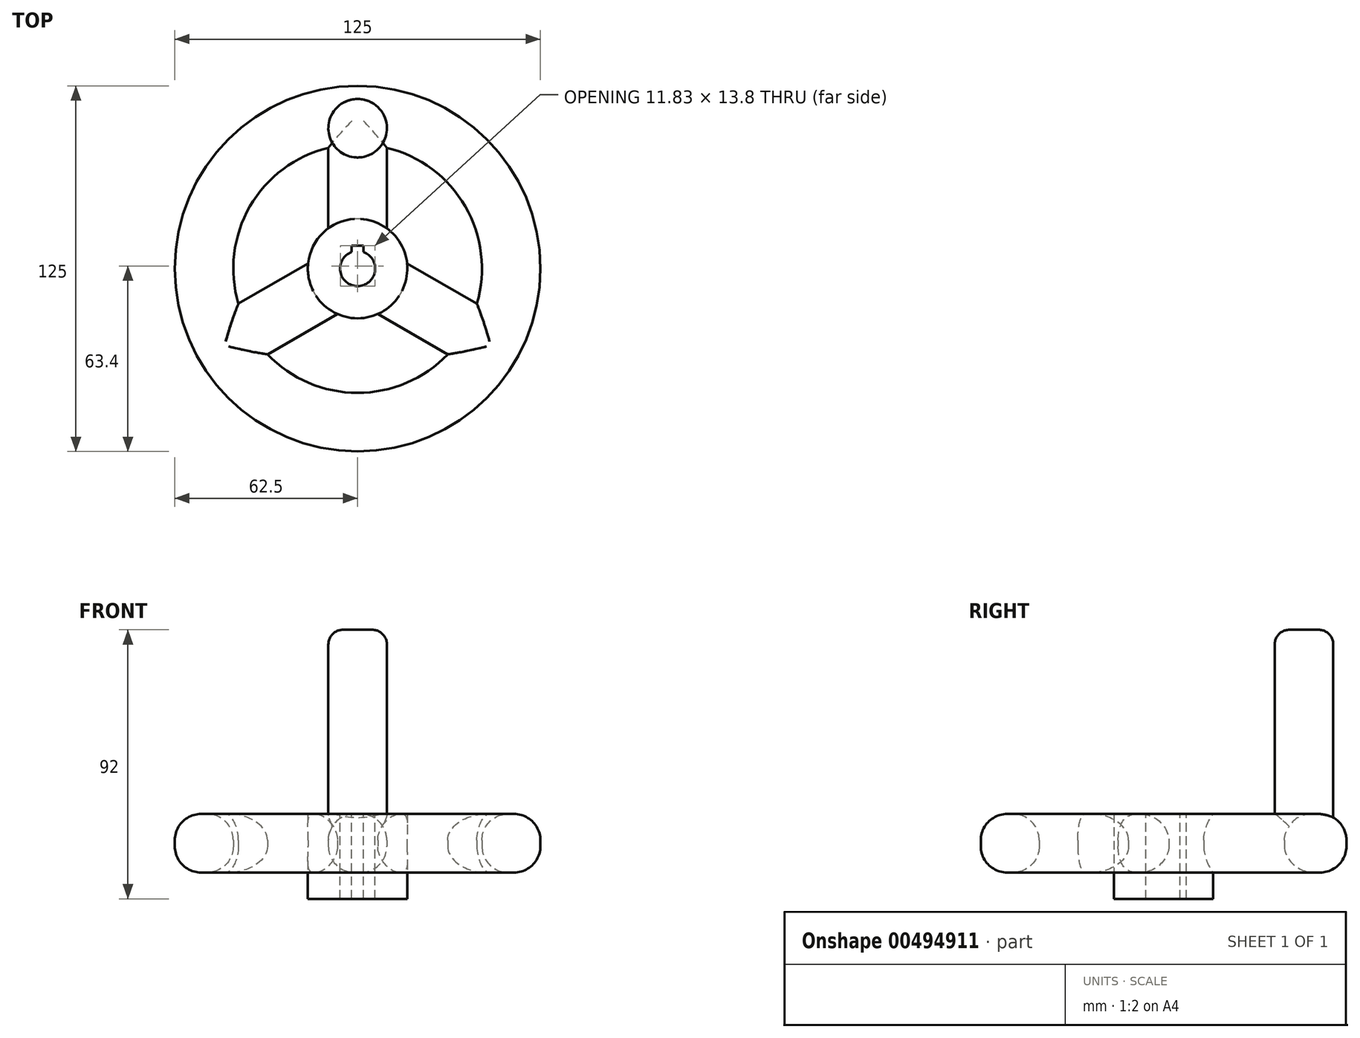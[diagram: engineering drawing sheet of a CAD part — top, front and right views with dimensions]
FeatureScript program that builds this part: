
annotation { "Feature Type Name" : "Feature", "Feature Type Description" : "" }
export const myFeature = defineFeature(function(context is Context, id is Id, definition is map)
    precondition{}
    {
        {
            var Q0;
            Q0=qCreatedBy(makeId("Top.planeOp"),FACE);
            var sketch = newSketch(context, id + "F0", { "sketchPlane" : qUnion([Q0])});
            skArc(sketch, "E0", {"start": v(-6.9, -15.53) * mm, "mid": v(0, -17) * mm, "end": v(6.9, -15.53) * mm});
            skArc(sketch, "E1", {"start": v(-30.77, -29.31) * mm, "mid": v(0, -42.5) * mm, "end": v(30.77, -29.31) * mm});
            skCircle(sketch, "E2", {"center": v(0, 0) * mm, "radius": 62.5 * mm});
            skLineSegment(sketch, "E3", {"start": v(-10, 41.3) * mm, "end": v(-10, 13.75) * mm});
            skLineSegment(sketch, "E4", {"start": v(10, 41.3) * mm, "end": v(10, 13.75) * mm});
            skLineSegment(sketch, "E5", {"start": v(-16.9, 1.79) * mm, "end": v(-40.77, -12) * mm});
            skLineSegment(sketch, "E6", {"start": v(-6.9, -15.53) * mm, "end": v(-30.77, -29.31) * mm});
            skLineSegment(sketch, "E7", {"start": v(6.9, -15.53) * mm, "end": v(30.77, -29.31) * mm});
            skLineSegment(sketch, "E8", {"start": v(16.9, 1.79) * mm, "end": v(40.77, -12) * mm});
            skArc(sketch, "E9.trimOffspring", {"start": v(-10, 13.75) * mm, "mid": v(-14.72, 8.5) * mm, "end": v(-16.9, 1.79) * mm});
            skArc(sketch, "E10.trimOffspring", {"start": v(-10, 41.3) * mm, "mid": v(-36.8, 21.25) * mm, "end": v(-40.77, -12) * mm});
            skArc(sketch, "E11.trimOffspring", {"start": v(40.77, -12) * mm, "mid": v(36.8, 21.25) * mm, "end": v(10, 41.3) * mm});
            skArc(sketch, "E12.trimOffspring", {"start": v(16.9, 1.79) * mm, "mid": v(14.72, 8.5) * mm, "end": v(10, 13.75) * mm});
            skSolve(sketch);
        }
        {
            var Q0;
            Q0=qSketchRegion(id+"F0",true);
            extrude(context, id + "F1", {"entities" : qUnion([Q0]), "depth" : 20 * mm});
        }
        {
            var Q0;
            Q0=makeQuery(id+"F1.opExtrude","CAP_EDGE",EDGE,{"disambiguationData":[OSD([sQuery(id+"F0.wireOp",EDGE,"E5")])],"isStart":false});
            var Q1;
            Q1=makeQuery(id+"F1.opExtrude","CAP_EDGE",EDGE,{"disambiguationData":[OSD([sQuery(id+"F0.wireOp",EDGE,"E8")])],"isStart":false});
            var Q2;
            Q2=makeQuery(id+"F1.opExtrude","CAP_EDGE",EDGE,{"disambiguationData":[OSD([sQuery(id+"F0.wireOp",EDGE,"E7")])],"isStart":false});
            var Q3;
            Q3=makeQuery(id+"F1.opExtrude","CAP_EDGE",EDGE,{"disambiguationData":[OSD([sQuery(id+"F0.wireOp",EDGE,"E6")])],"isStart":false});
            var Q4;
            Q4=makeQuery(id+"F1.opExtrude","CAP_EDGE",EDGE,{"disambiguationData":[OSD([sQuery(id+"F0.wireOp",EDGE,"E1")])],"isStart":false});
            var Q5;
            Q5=makeQuery(id+"F1.opExtrude","CAP_EDGE",EDGE,{"disambiguationData":[OSD([sQuery(id+"F0.wireOp",EDGE,"E5")])],"isStart":true});
            var Q6;
            Q6=makeQuery(id+"F1.opExtrude","CAP_EDGE",EDGE,{"disambiguationData":[OSD([sQuery(id+"F0.wireOp",EDGE,"E6")])],"isStart":true});
            var Q7;
            Q7=makeQuery(id+"F1.opExtrude","CAP_EDGE",EDGE,{"disambiguationData":[OSD([sQuery(id+"F0.wireOp",EDGE,"E8")])],"isStart":true});
            var Q8;
            Q8=makeQuery(id+"F1.opExtrude","CAP_EDGE",EDGE,{"disambiguationData":[OSD([sQuery(id+"F0.wireOp",EDGE,"E7")])],"isStart":true});
            var Q9;
            Q9=makeQuery(id+"F1.opExtrude","CAP_EDGE",EDGE,{"disambiguationData":[OSD([sQuery(id+"F0.wireOp",EDGE,"E4")])],"isStart":true});
            var Q10;
            Q10=makeQuery(id+"F1.opExtrude","CAP_EDGE",EDGE,{"disambiguationData":[OSD([sQuery(id+"F0.wireOp",EDGE,"E3")])],"isStart":true});
            var Q11;
            Q11=makeQuery(id+"F1.opExtrude","CAP_EDGE",EDGE,{"disambiguationData":[OSD([sQuery(id+"F0.wireOp",EDGE,"E10.trimOffspring")])],"isStart":false});
            var Q12;
            Q12=makeQuery(id+"F1.opExtrude","CAP_EDGE",EDGE,{"disambiguationData":[OSD([sQuery(id+"F0.wireOp",EDGE,"E3")])],"isStart":false});
            var Q13;
            Q13=makeQuery(id+"F1.opExtrude","CAP_EDGE",EDGE,{"disambiguationData":[OSD([sQuery(id+"F0.wireOp",EDGE,"E4")])],"isStart":false});
            var Q14;
            Q14=makeQuery(id+"F1.opExtrude","CAP_EDGE",EDGE,{"disambiguationData":[OSD([sQuery(id+"F0.wireOp",EDGE,"E11.trimOffspring")])],"isStart":false});
            var Q15;
            Q15=makeQuery(id+"F1.opExtrude","CAP_EDGE",EDGE,{"disambiguationData":[OSD([sQuery(id+"F0.wireOp",EDGE,"E11.trimOffspring")])],"isStart":true});
            var Q16;
            Q16=makeQuery(id+"F1.opExtrude","CAP_EDGE",EDGE,{"disambiguationData":[OSD([sQuery(id+"F0.wireOp",EDGE,"E10.trimOffspring")])],"isStart":true});
            var Q17;
            Q17=makeQuery(id+"F1.opExtrude","CAP_EDGE",EDGE,{"disambiguationData":[OSD([sQuery(id+"F0.wireOp",EDGE,"E2")])],"isStart":false});
            var Q18;
            Q18=makeQuery(id+"F1.opExtrude","CAP_EDGE",EDGE,{"disambiguationData":[OSD([sQuery(id+"F0.wireOp",EDGE,"E2")])],"isStart":true});
            var Q19;
            Q19=makeQuery(id+"F1.opExtrude","CAP_EDGE",EDGE,{"disambiguationData":[OSD([sQuery(id+"F0.wireOp",EDGE,"E1")])],"isStart":true});
            fillet(context, id + "F2", {"entities" : qUnion([Q0, Q1, Q2, Q3, Q4, Q5, Q6, Q7, Q8, Q9, Q10, Q11, Q12, Q13, Q14, Q15, Q16, Q17, Q18, Q19]), "radius" : 9 * mm, "tangentPropagation" : true, "allowEdgeOverflow" : false});
        }
        {
            var Q0;
            Q0=makeQuery(id+"F1.opExtrude","CAP_FACE",FACE,{"disambiguationData":[OSD([sQuery(id+"F0.wireOp",EDGE,"qARPkjHC-YAaQ-jKnd-qtzr-ODSBI9HnrwAN"),sQuery(id+"F0.wireOp",EDGE,"E0"),sQuery(id+"F0.wireOp",EDGE,"E1"),sQuery(id+"F0.wireOp",EDGE,"E2"),sQuery(id+"F0.wireOp",EDGE,"E3"),sQuery(id+"F0.wireOp",EDGE,"E4"),sQuery(id+"F0.wireOp",EDGE,"E5"),sQuery(id+"F0.wireOp",EDGE,"E6"),sQuery(id+"F0.wireOp",EDGE,"E7"),sQuery(id+"F0.wireOp",EDGE,"E8"),sQuery(id+"F0.wireOp",EDGE,"E9.trimOffspring"),sQuery(id+"F0.wireOp",EDGE,"E10.trimOffspring"),sQuery(id+"F0.wireOp",EDGE,"E11.trimOffspring"),sQuery(id+"F0.wireOp",EDGE,"E12.trimOffspring")])],"isStart":true});
            var sketch = newSketch(context, id + "F3", { "sketchPlane" : qUnion([Q0])});
            skCircle(sketch, "E13", {"center": v(0, 0) * mm, "radius": 17 * mm});
            skSolve(sketch);
        }
        {
            var Q0;
            Q0=qSketchRegion(id+"F3",true);
            extrude(context, id + "F4", {"entities" : qUnion([Q0]), "operationType" : NewBodyOperationType.ADD, "depth" : 9 * mm});
        }
        {
            var Q0;
            Q0=makeQuery(id+"F1.opExtrude","CAP_FACE",FACE,{"disambiguationData":[OSD([sQuery(id+"F0.wireOp",EDGE,"E0"),sQuery(id+"F0.wireOp",EDGE,"E1"),sQuery(id+"F0.wireOp",EDGE,"E2"),sQuery(id+"F0.wireOp",EDGE,"E3"),sQuery(id+"F0.wireOp",EDGE,"E4"),sQuery(id+"F0.wireOp",EDGE,"E5"),sQuery(id+"F0.wireOp",EDGE,"E6"),sQuery(id+"F0.wireOp",EDGE,"E7"),sQuery(id+"F0.wireOp",EDGE,"E8"),sQuery(id+"F0.wireOp",EDGE,"E9.trimOffspring"),sQuery(id+"F0.wireOp",EDGE,"E10.trimOffspring"),sQuery(id+"F0.wireOp",EDGE,"E11.trimOffspring"),sQuery(id+"F0.wireOp",EDGE,"E12.trimOffspring")])],"isStart":false});
            var sketch = newSketch(context, id + "F5", { "sketchPlane" : qUnion([Q0])});
            skCircle(sketch, "E14", {"center": v(0, 48) * mm, "radius": 10 * mm});
            skSolve(sketch);
        }
        {
            var Q0;
            Q0=qSketchRegion(id+"F5",true);
            extrude(context, id + "F6", {"entities" : qUnion([Q0]), "operationType" : NewBodyOperationType.ADD, "depth" : 63 * mm, "hasSecondDirection" : true, "secondDirectionOppositeDirection" : true, "secondDirectionDepth" : 5 * mm});
        }
        {
            var Q0;
            Q0=makeQuery(id+"F1.opExtrude","CAP_FACE",FACE,{"disambiguationData":[OSD([sQuery(id+"F0.wireOp",EDGE,"E0"),sQuery(id+"F0.wireOp",EDGE,"E1"),sQuery(id+"F0.wireOp",EDGE,"E2"),sQuery(id+"F0.wireOp",EDGE,"E3"),sQuery(id+"F0.wireOp",EDGE,"E4"),sQuery(id+"F0.wireOp",EDGE,"E5"),sQuery(id+"F0.wireOp",EDGE,"E6"),sQuery(id+"F0.wireOp",EDGE,"E7"),sQuery(id+"F0.wireOp",EDGE,"E8"),sQuery(id+"F0.wireOp",EDGE,"E9.trimOffspring"),sQuery(id+"F0.wireOp",EDGE,"E10.trimOffspring"),sQuery(id+"F0.wireOp",EDGE,"E11.trimOffspring"),sQuery(id+"F0.wireOp",EDGE,"E12.trimOffspring")])],"isStart":false});
            var sketch = newSketch(context, id + "F7", { "sketchPlane" : qUnion([Q0])});
            skCircle(sketch, "E15", {"center": v(0, 0) * mm, "radius": 6 * mm});
            skSolve(sketch);
        }
        {
            var Q0;
            Q0=qSketchRegion(id+"F7",true);
            extrude(context, id + "F8", {"entities" : qUnion([Q0]), "operationType" : NewBodyOperationType.REMOVE, "endBound" : BoundingType.THROUGH_ALL, "oppositeDirection" : true, "depth" : 25 * mm});
        }
        {
            var Q0;
            Q0=makeQuery(id+"F1.opExtrude","CAP_FACE",FACE,{"disambiguationData":[OSD([sQuery(id+"F0.wireOp",EDGE,"E0"),sQuery(id+"F0.wireOp",EDGE,"E1"),sQuery(id+"F0.wireOp",EDGE,"E2"),sQuery(id+"F0.wireOp",EDGE,"E3"),sQuery(id+"F0.wireOp",EDGE,"E4"),sQuery(id+"F0.wireOp",EDGE,"E5"),sQuery(id+"F0.wireOp",EDGE,"E6"),sQuery(id+"F0.wireOp",EDGE,"E7"),sQuery(id+"F0.wireOp",EDGE,"E8"),sQuery(id+"F0.wireOp",EDGE,"E9.trimOffspring"),sQuery(id+"F0.wireOp",EDGE,"E10.trimOffspring"),sQuery(id+"F0.wireOp",EDGE,"E11.trimOffspring"),sQuery(id+"F0.wireOp",EDGE,"E12.trimOffspring")])],"isStart":false});
            var sketch = newSketch(context, id + "F9", { "sketchPlane" : qUnion([Q0])});
            skLineSegment(sketch, "E16.bottom", {"start": v(-2, 0) * mm, "end": v(2, 0) * mm});
            skLineSegment(sketch, "E16.top", {"start": v(-2, 7.8) * mm, "end": v(2, 7.8) * mm});
            skLineSegment(sketch, "E16.left", {"start": v(-2, 0) * mm, "end": v(-2, 7.8) * mm});
            skLineSegment(sketch, "E16.right", {"start": v(2, 0) * mm, "end": v(2, 7.8) * mm});
            skSolve(sketch);
        }
        {
            var Q0;
            Q0=qSketchRegion(id+"F9",true);
            extrude(context, id + "F10", {"entities" : qUnion([Q0]), "operationType" : NewBodyOperationType.REMOVE, "endBound" : BoundingType.THROUGH_ALL, "oppositeDirection" : true, "depth" : 25 * mm});
        }
        {
            var Q0;
            Q0=makeQuery(id+"F6.opExtrude","CAP_EDGE",EDGE,{"disambiguationData":[OSD([sQuery(id+"F5.wireOp",EDGE,"E14")])],"isStart":false});
            fillet(context, id + "F11", {"entities" : qUnion([Q0]), "radius" : 5 * mm, "tangentPropagation" : true, "allowEdgeOverflow" : false});
        }
    });
